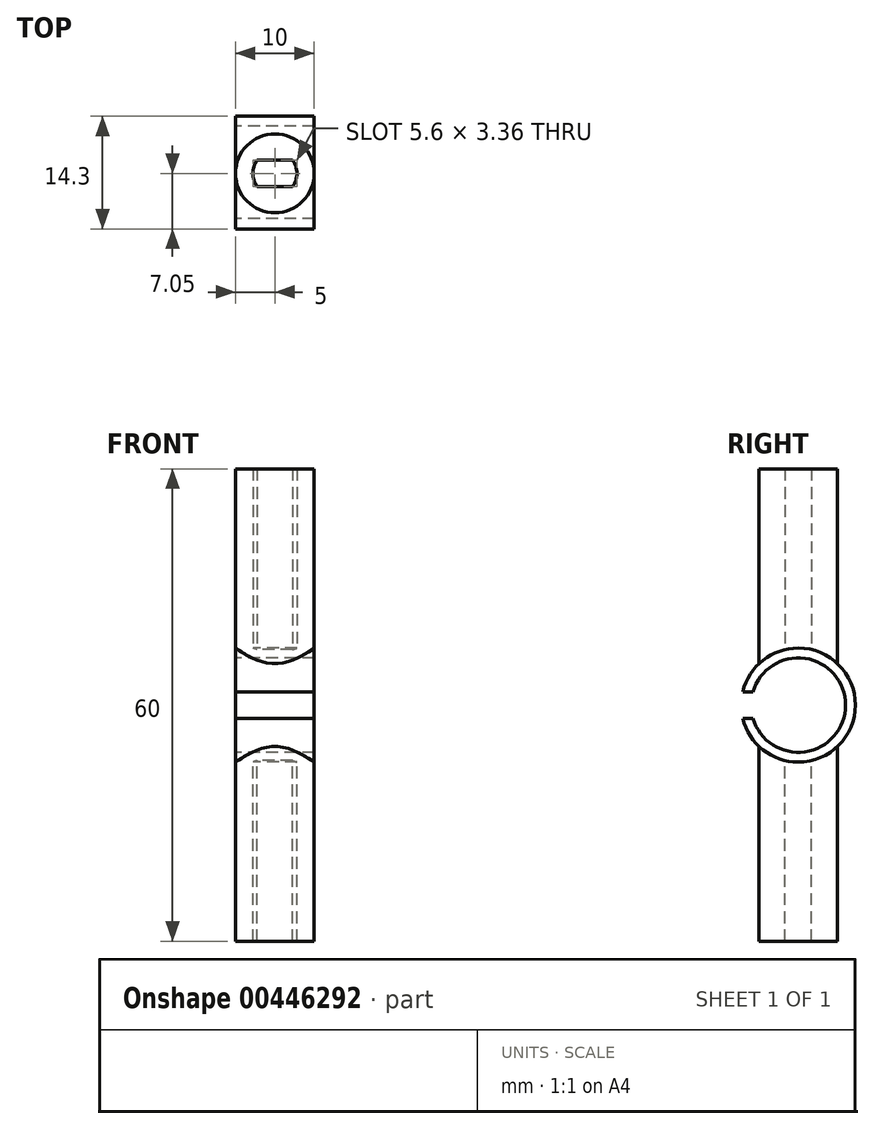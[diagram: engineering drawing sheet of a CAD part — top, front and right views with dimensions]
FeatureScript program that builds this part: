
annotation { "Feature Type Name" : "Feature", "Feature Type Description" : "" }
export const myFeature = defineFeature(function(context is Context, id is Id, definition is map)
    precondition{}
    {
        {
            var Q0;
            Q0=qCreatedBy(makeId("Top.planeOp"),FACE);
            var sketch = newSketch(context, id + "F0", { "sketchPlane" : qUnion([Q0])});
            skArc(sketch, "E0", {"start": v(2.24, -1.68) * mm, "mid": v(2.8, 0) * mm, "end": v(2.24, 1.68) * mm});
            skLineSegment(sketch, "E1.bottom", {"start": v(2.24, 1.68) * mm, "end": v(-2.24, 1.68) * mm});
            skLineSegment(sketch, "E1.top", {"start": v(2.24, -1.68) * mm, "end": v(-2.24, -1.68) * mm});
            skCircle(sketch, "E2", {"center": v(0, 0) * mm, "radius": 5 * mm});
            skArc(sketch, "E3.trimOffspring", {"start": v(-2.24, 1.68) * mm, "mid": v(-2.8, 0) * mm, "end": v(-2.24, -1.68) * mm});
            skSolve(sketch);
        }
        {
            var Q0;
            Q0=makeQuery(id+"F0.imprint","IMPRINT",FACE,{"disambiguationData":[TD([[makeQuery(id+"F0.imprint","IMPRINT",EDGE,{"derivedFrom":sQuery(id+"F0.wireOp",EDGE,"E0")}),-1.0]])]});
            extrude(context, id + "F1", {"entities" : qUnion([Q0]), "depth" : 30 * mm});
        }
        {
            var Q0;
            Q0=makeQuery(id+"F0.imprint","IMPRINT",FACE,{"disambiguationData":[TD([[makeQuery(id+"F0.imprint","IMPRINT",EDGE,{"derivedFrom":sQuery(id+"F0.wireOp",EDGE,"E0")}),1.0]])]});
            extrude(context, id + "F2", {"entities" : qUnion([Q0]), "operationType" : NewBodyOperationType.ADD, "depth" : 5 * mm});
        }
        {
            var Q0;
            Q0=qCreatedBy(makeId("Right.planeOp"),FACE);
            var sketch = newSketch(context, id + "F3", { "sketchPlane" : qUnion([Q0])});
            skCircle(sketch, "E4", {"center": v(0, 0) * mm, "radius": 7.25 * mm});
            skCircle(sketch, "E5", {"center": v(0, 0) * mm, "radius": 6 * mm});
            skLineSegment(sketch, "E6", {"start": v(0, 0) * mm, "end": v(-18.1, 0) * mm, "construction": true});
            skLineSegment(sketch, "E7.bottom", {"start": v(-7.87, 1.68) * mm, "end": v(-5.16, 1.68) * mm});
            skLineSegment(sketch, "E7.top", {"start": v(-7.87, -1.68) * mm, "end": v(-5.16, -1.68) * mm});
            skLineSegment(sketch, "E7.left", {"start": v(-7.87, 1.68) * mm, "end": v(-7.87, -1.68) * mm});
            skLineSegment(sketch, "E7.right", {"start": v(-5.16, 1.68) * mm, "end": v(-5.16, -1.68) * mm});
            skPoint(sketch, "E7.middle", {"position": v(-6.52, 0) * mm});
            skSolve(sketch);
        }
        {
            var Q0;
            Q0=makeQuery(id+"F3.imprint","IMPRINT",FACE,{"disambiguationData":[TD([[makeQuery(id+"F3.imprint","IMPRINT",EDGE,{"derivedFrom":sQuery(id+"F3.wireOp",EDGE,"E5")}),1.0]])]});
            var Q1;
            {var subQ0=sQuery(id+"F3.wireOp",EDGE,"h8HDv5gG-uclH-0vFo-wMJO-JodwiMFUr1mN.bottom");Q1=makeQuery(id+"F3.imprint","IMPRINT",FACE,{"disambiguationData":[TD([[makeQuery(id+"F3.imprint","IMPRINT",EDGE,{"derivedFrom":subQ0}),1.0]])]});}
            extrude(context, id + "F4", {"entities" : qUnion([Q0, Q1]), "operationType" : NewBodyOperationType.REMOVE, "oppositeDirection" : true, "depth" : 30 * mm, "hasSecondDirection" : true, "secondDirectionOppositeDirection" : false, "secondDirectionDepth" : 30 * mm});
        }
        {
            var Q0;
            {var subQ0=sQuery(id+"F3.wireOp",EDGE,"E7.bottom");var subQ1=sQuery(id+"F3.wireOp",EDGE,"E4");var subQ2=makeQuery(id+"F3.imprint","INTERSECT",VERTEX,{"derivedFrom":[subQ1,subQ0]});Q0=makeQuery(id+"F3.imprint","IMPRINT",FACE,{"disambiguationData":[TD([[makeQuery(id+"F3.imprint","IMPRINT",EDGE,{"disambiguationData":[TD([[subQ2,1.0]])],"derivedFrom":subQ1}),1.0]])]});}
            var Q1;
            {var subQ0=sQuery(id+"F3.wireOp",EDGE,"E7.bottom");var subQ1=sQuery(id+"F3.wireOp",EDGE,"E4");var subQ2=makeQuery(id+"F3.imprint","INTERSECT",VERTEX,{"derivedFrom":[subQ1,subQ0]});Q1=makeQuery(id+"F3.imprint","IMPRINT",FACE,{"disambiguationData":[TD([[makeQuery(id+"F3.imprint","IMPRINT",EDGE,{"disambiguationData":[TD([[subQ2,1.0]])],"derivedFrom":subQ1}),1.0]])]});}
            var Q2;
            {var subQ0=sQuery(id+"F3.wireOp",EDGE,"E7.bottom");var subQ1=sQuery(id+"F3.wireOp",EDGE,"E4");var subQ2=makeQuery(id+"F3.imprint","INTERSECT",VERTEX,{"derivedFrom":[subQ1,subQ0]});Q2=makeQuery(id+"F3.imprint","IMPRINT",FACE,{"disambiguationData":[TD([[makeQuery(id+"F3.imprint","IMPRINT",EDGE,{"disambiguationData":[TD([[subQ2,1.0]])],"derivedFrom":subQ1}),1.0]])]});}
            extrude(context, id + "F5", {"entities" : qUnion([Q0, Q1, Q2]), "depth" : 5 * mm, "hasSecondDirection" : true, "secondDirectionOppositeDirection" : true, "secondDirectionDepth" : 5 * mm});
        }
        {
            var Q0;
            Q0=makeQuery(id+"F1.opExtrude","SWEPT_BODY",BODY,{"disambiguationData":[OSD([sQuery(id+"F0.wireOp",EDGE,"E0"),sQuery(id+"F0.wireOp",EDGE,"E1.bottom"),sQuery(id+"F0.wireOp",EDGE,"E1.top"),sQuery(id+"F0.wireOp",EDGE,"E2"),sQuery(id+"F0.wireOp",EDGE,"E3.trimOffspring")])]});
            var Q1;
            Q1=qCreatedBy(makeId("Top.planeOp"),FACE);
            mirror(context, id + "F6", {"operationType" : NewBodyOperationType.ADD, "entities" : qUnion([Q0]), "mirrorPlane" : qUnion([Q1])});
        }
    });
